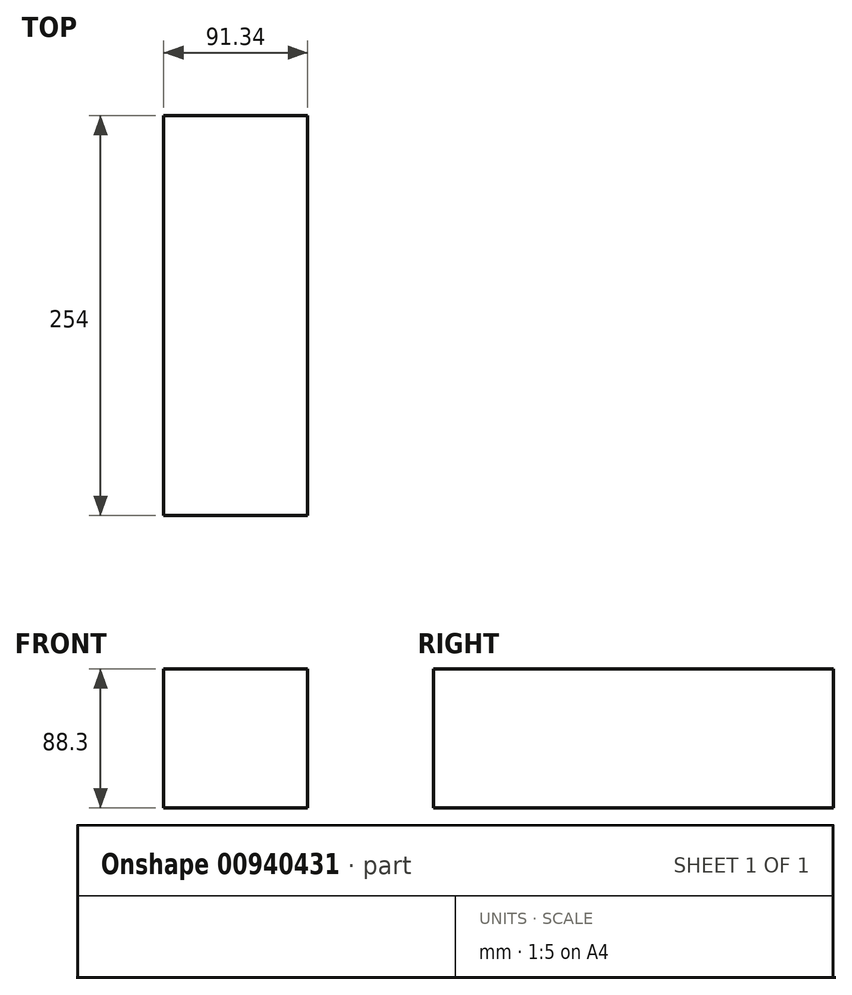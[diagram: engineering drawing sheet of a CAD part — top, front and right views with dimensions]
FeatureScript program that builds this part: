
annotation { "Feature Type Name" : "Feature", "Feature Type Description" : "" }
export const myFeature = defineFeature(function(context is Context, id is Id, definition is map)
    precondition{}
    {
        {
            var Q0;
            Q0=qCreatedBy(makeId("Front.planeOp"),FACE);
            var sketch = newSketch(context, id + "F0", { "sketchPlane" : qUnion([Q0])});
            skLineSegment(sketch, "E0.bottom", {"start": v(41.73, -41.94) * mm, "end": v(-49.6, -41.94) * mm});
            skLineSegment(sketch, "E0.top", {"start": v(41.73, 46.36) * mm, "end": v(-49.6, 46.36) * mm});
            skLineSegment(sketch, "E0.left", {"start": v(41.73, -41.94) * mm, "end": v(41.73, 46.36) * mm});
            skLineSegment(sketch, "E0.right", {"start": v(-49.6, -41.94) * mm, "end": v(-49.6, 46.36) * mm});
            skSolve(sketch);
        }
        {
            var Q0;
            Q0 = qSketchRegion(id + "F0", true);
            extrude(context, id + "F1", {"entities" : qUnion([Q0]), "depth" : 254 * mm, "offsetDistance" : 25.4 * mm});
        }
    });
